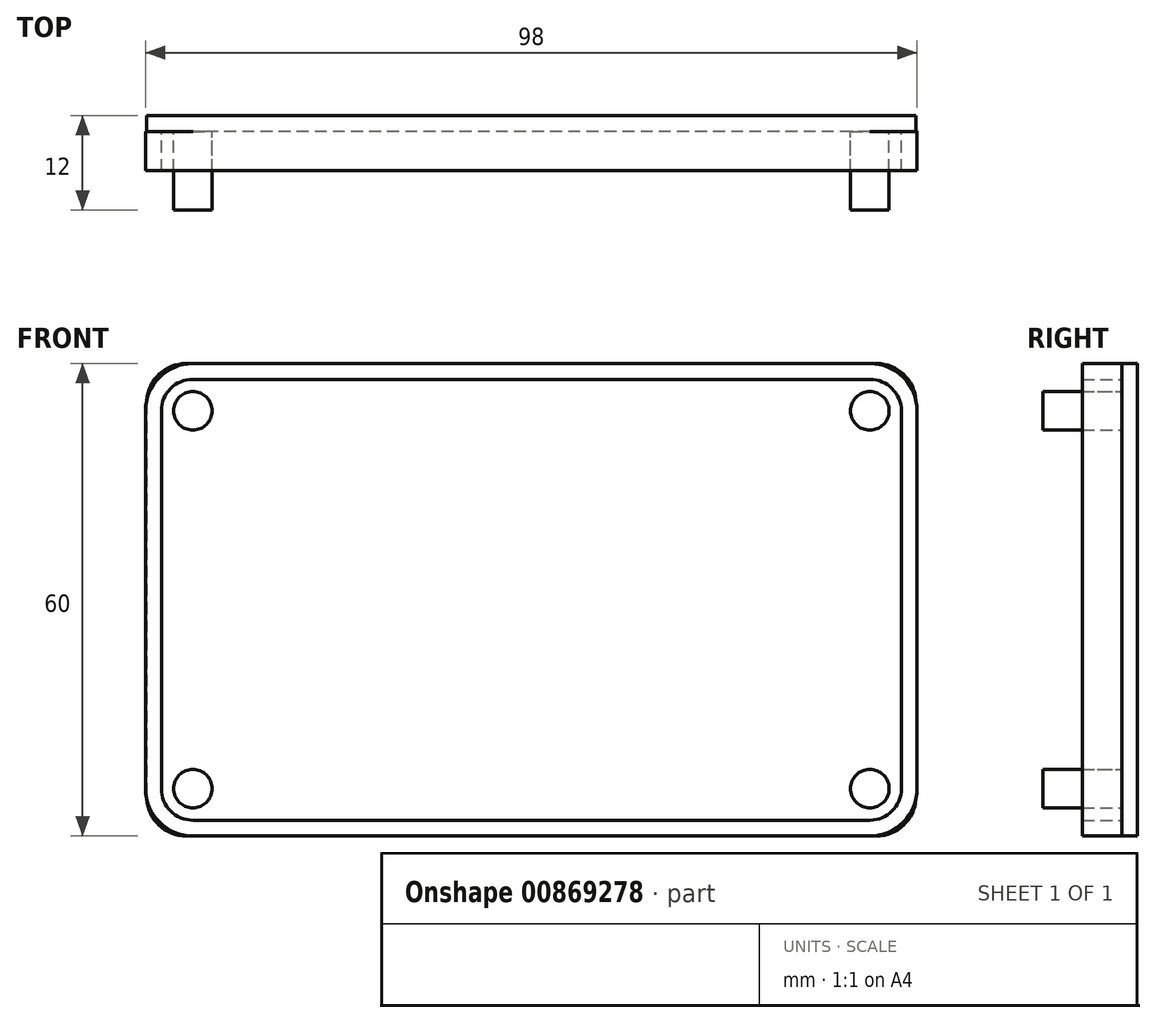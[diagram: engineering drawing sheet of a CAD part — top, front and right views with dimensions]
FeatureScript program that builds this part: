
annotation { "Feature Type Name" : "Feature", "Feature Type Description" : "" }
export const myFeature = defineFeature(function(context is Context, id is Id, definition is map)
    precondition{}
    {
        {
            var Q0;
            Q0=qCreatedBy(makeId("Front.planeOp"),FACE);
            var sketch = newSketch(context, id + "F0", { "sketchPlane" : qUnion([Q0])});
            skLineSegment(sketch, "E0.bottom", {"start": v(43, -28) * mm, "end": v(-43, -28) * mm});
            skLineSegment(sketch, "E0.top", {"start": v(43, 28) * mm, "end": v(-43, 28) * mm});
            skLineSegment(sketch, "E0.left", {"start": v(47, -24) * mm, "end": v(47, 24) * mm});
            skLineSegment(sketch, "E0.right", {"start": v(-47, -24) * mm, "end": v(-47, 24) * mm});
            skPoint(sketch, "E0.middle", {"position": v(0, 0) * mm});
            skPoint(sketch, "E1.visualSharp", {"position": v(-47, 28) * mm});
            skArc(sketch, "E1.filletArc", {"start": v(-43, 28) * mm, "mid": v(-45.83, 26.83) * mm, "end": v(-47, 24) * mm});
            skPoint(sketch, "E2.visualSharp", {"position": v(-47, -28) * mm});
            skArc(sketch, "E2.filletArc", {"start": v(-47, -24) * mm, "mid": v(-45.83, -26.83) * mm, "end": v(-43, -28) * mm});
            skPoint(sketch, "E3.visualSharp", {"position": v(47, -28) * mm});
            skArc(sketch, "E3.filletArc", {"start": v(43, -28) * mm, "mid": v(45.83, -26.83) * mm, "end": v(47, -24) * mm});
            skPoint(sketch, "E4.visualSharp", {"position": v(47, 28) * mm});
            skArc(sketch, "E4.filletArc", {"start": v(47, 24) * mm, "mid": v(45.83, 26.83) * mm, "end": v(43, 28) * mm});
            skLineSegment(sketch, "E5.0", {"start": v(43, 30) * mm, "end": v(-43, 30) * mm});
            skArc(sketch, "E5.1", {"start": v(49, 24) * mm, "mid": v(47.24, 28.24) * mm, "end": v(43, 30) * mm});
            skArc(sketch, "E5.2", {"start": v(-43, 30) * mm, "mid": v(-47.24, 28.24) * mm, "end": v(-49, 24) * mm});
            skLineSegment(sketch, "E5.3", {"start": v(49, -24) * mm, "end": v(49, 24) * mm});
            skLineSegment(sketch, "E5.4", {"start": v(-49, -24) * mm, "end": v(-49, 24) * mm});
            skArc(sketch, "E5.5", {"start": v(-49, -24) * mm, "mid": v(-47.24, -28.24) * mm, "end": v(-43, -30) * mm});
            skLineSegment(sketch, "E5.6", {"start": v(43, -30) * mm, "end": v(-43, -30) * mm});
            skArc(sketch, "E5.7", {"start": v(43, -30) * mm, "mid": v(47.24, -28.24) * mm, "end": v(49, -24) * mm});
            skSolve(sketch);
        }
        {
            var Q0;
            Q0=qCreatedBy(makeId("Front.planeOp"),FACE);
            var sketch = newSketch(context, id + "F1", { "sketchPlane" : qUnion([Q0])});
            skCircle(sketch, "E6", {"center": v(-43, 24) * mm, "radius": 2.45 * mm});
            skCircle(sketch, "E7", {"center": v(-43, -24) * mm, "radius": 2.45 * mm});
            skCircle(sketch, "E8", {"center": v(43, -24) * mm, "radius": 2.45 * mm});
            skCircle(sketch, "E9", {"center": v(43, 24) * mm, "radius": 2.45 * mm});
            skSolve(sketch);
        }
        {
            var Q0;
            Q0 = qSketchRegion(id + "F1", true);
            extrude(context, id + "F2", {"entities" : qUnion([Q0]), "depth" : 10 * mm, "offsetDistance" : 25 * mm});
        }
        {
            var Q0;
            Q0 = qSketchRegion(id + "F0", true);
            extrude(context, id + "F3", {"entities" : qUnion([Q0]), "depth" : 5 * mm, "offsetDistance" : 25 * mm});
        }
        {
            var Q0;
            Q0=makeQuery(id+"F3.opExtrude","CAP_FACE",FACE,{"disambiguationData":[OSD([sQuery(id+"F0.wireOp",EDGE,"E0.bottom"),sQuery(id+"F0.wireOp",EDGE,"E0.top"),sQuery(id+"F0.wireOp",EDGE,"E0.left"),sQuery(id+"F0.wireOp",EDGE,"E0.right"),sQuery(id+"F0.wireOp",EDGE,"E1.filletArc"),sQuery(id+"F0.wireOp",EDGE,"E2.filletArc"),sQuery(id+"F0.wireOp",EDGE,"E3.filletArc"),sQuery(id+"F0.wireOp",EDGE,"E4.filletArc"),sQuery(id+"F0.wireOp",EDGE,"E5.0"),sQuery(id+"F0.wireOp",EDGE,"E5.1"),sQuery(id+"F0.wireOp",EDGE,"E5.2"),sQuery(id+"F0.wireOp",EDGE,"E5.3"),sQuery(id+"F0.wireOp",EDGE,"E5.4"),sQuery(id+"F0.wireOp",EDGE,"E5.5"),sQuery(id+"F0.wireOp",EDGE,"E5.6"),sQuery(id+"F0.wireOp",EDGE,"E5.7")])],"isStart":true});
            var sketch = newSketch(context, id + "F4", { "sketchPlane" : qUnion([Q0])});
            skLineSegment(sketch, "E10.bottom", {"start": v(-43.86, 30) * mm, "end": v(43.86, 30) * mm});
            skLineSegment(sketch, "E10.top", {"start": v(-43.86, -30) * mm, "end": v(43.86, -30) * mm});
            skLineSegment(sketch, "E10.left", {"start": v(-48.86, 25) * mm, "end": v(-48.86, -25) * mm});
            skLineSegment(sketch, "E10.right", {"start": v(48.86, 25) * mm, "end": v(48.86, -25) * mm});
            skPoint(sketch, "E10.middle", {"position": v(0, 0) * mm});
            skPoint(sketch, "E11.visualSharp", {"position": v(48.86, -30) * mm});
            skArc(sketch, "E11.filletArc", {"start": v(43.86, -30) * mm, "mid": v(47.4, -28.54) * mm, "end": v(48.86, -25) * mm});
            skPoint(sketch, "E12.visualSharp", {"position": v(48.86, 30) * mm});
            skArc(sketch, "E12.filletArc", {"start": v(48.86, 25) * mm, "mid": v(47.4, 28.54) * mm, "end": v(43.86, 30) * mm});
            skPoint(sketch, "E13.visualSharp", {"position": v(-48.86, 30) * mm});
            skArc(sketch, "E13.filletArc", {"start": v(-43.86, 30) * mm, "mid": v(-47.4, 28.54) * mm, "end": v(-48.86, 25) * mm});
            skPoint(sketch, "E14.visualSharp", {"position": v(-48.86, -30) * mm});
            skArc(sketch, "E14.filletArc", {"start": v(-48.86, -25) * mm, "mid": v(-47.4, -28.54) * mm, "end": v(-43.86, -30) * mm});
            skSolve(sketch);
        }
        {
            var Q0;
            Q0 = qSketchRegion(id + "F4", true);
            extrude(context, id + "F5", {"entities" : qUnion([Q0]), "operationType" : NewBodyOperationType.ADD, "depth" : 2 * mm, "offsetDistance" : 25 * mm});
        }
    });
